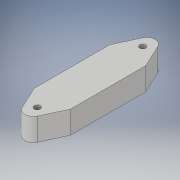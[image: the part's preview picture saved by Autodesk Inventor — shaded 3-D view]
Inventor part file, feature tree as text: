
AUTODESK INVENTOR PART (.ipt)
format: ipt  version: 2019 (Build 230136000, 136)  size: 135,680 bytes
history: native  units: mm
features: sketch x3, extrude x2, hole x1
ambient origin geometry x8: Origin, YZ Plane, XZ Plane, XY Plane, X Axis, Y Axis, Z Axis, Center Point
bodies: Solid1 (feature_tree)
feature tree (6):
  sketch  "Sketch1"  dims[d0=15.0mm d1=20.0mm]
  extrude  "Extrusion1"  Depth=20.0mm
  extrude  "Extrusion2"  Depth=20.0mm
  hole  "Hole1"  [1 undecoded]
  sketch  "Sketch2"  dims[d2=15.0mm d3=20.0mm]
  sketch  "Sketch3"  dims[d4=12.0mm d5=12.0mm d6=25.0mm d7=25.0mm d8=15.0mm d9=7.0mm d10=15.0mm d11=7.0mm d12=15.0mm d13=0.0mm d14=10.0mm d15=0.0mm d16=35.0mm d17=35.0mm d18=4.0mm d19=6.0mm d20=5.0mm d21=2.0mm d22=90.0deg d23=8.0mm d24=20.594885mm d25=0.0625mm d26=0.75mm d27=0.375mm]
note: 1 required parameter value undecoded (feature->parameter linkage not recoverable at this tier; creation-order binding heuristic only, values carry confidence <= 0.55)
